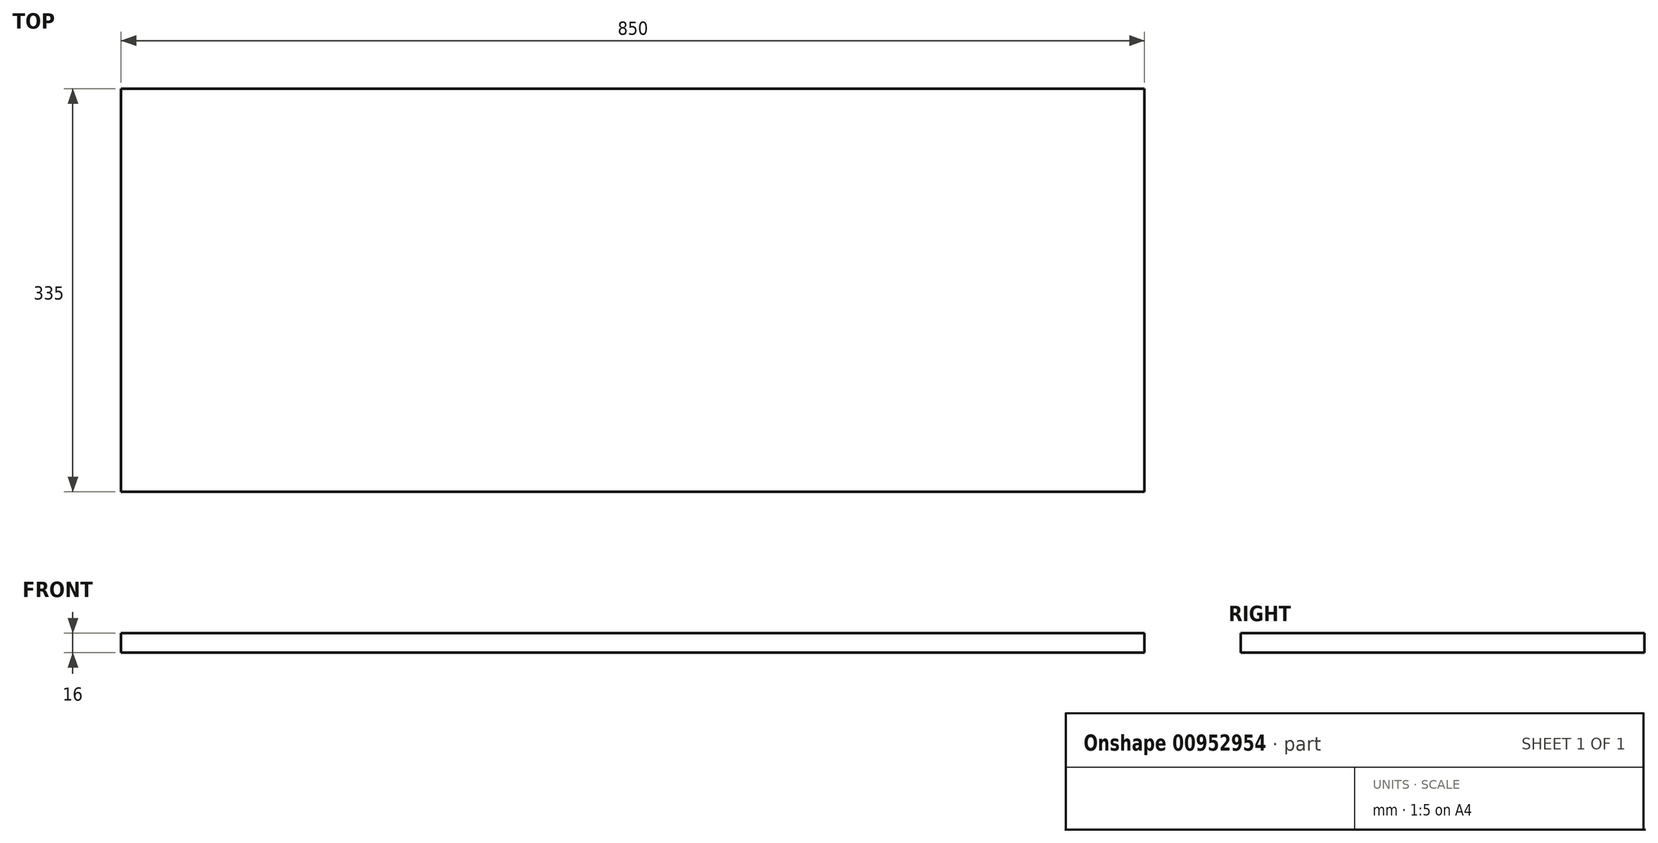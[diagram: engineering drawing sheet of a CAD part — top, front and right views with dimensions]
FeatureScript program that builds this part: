
annotation { "Feature Type Name" : "Feature", "Feature Type Description" : "" }
export const myFeature = defineFeature(function(context is Context, id is Id, definition is map)
    precondition{}
    {
        {
            var Q0;
            Q0=qCreatedBy(makeId("Top.planeOp"),FACE);
            var sketch = newSketch(context, id + "F0", { "sketchPlane" : qUnion([Q0])});
            skLineSegment(sketch, "E0.bottom", {"start": v(-318.72, 132.06) * mm, "end": v(531.28, 132.06) * mm});
            skLineSegment(sketch, "E0.top", {"start": v(-318.72, -202.94) * mm, "end": v(531.28, -202.94) * mm});
            skLineSegment(sketch, "E0.left", {"start": v(-318.72, 132.06) * mm, "end": v(-318.72, -202.94) * mm});
            skLineSegment(sketch, "E0.right", {"start": v(531.28, 132.06) * mm, "end": v(531.28, -202.94) * mm});
            skSolve(sketch);
        }
        {
            var Q0;
            Q0 = qSketchRegion(id + "F0", true);
            extrude(context, id + "F1", {"entities" : qUnion([Q0]), "depth" : 16 * mm, "offsetDistance" : 25 * mm});
        }
    });
